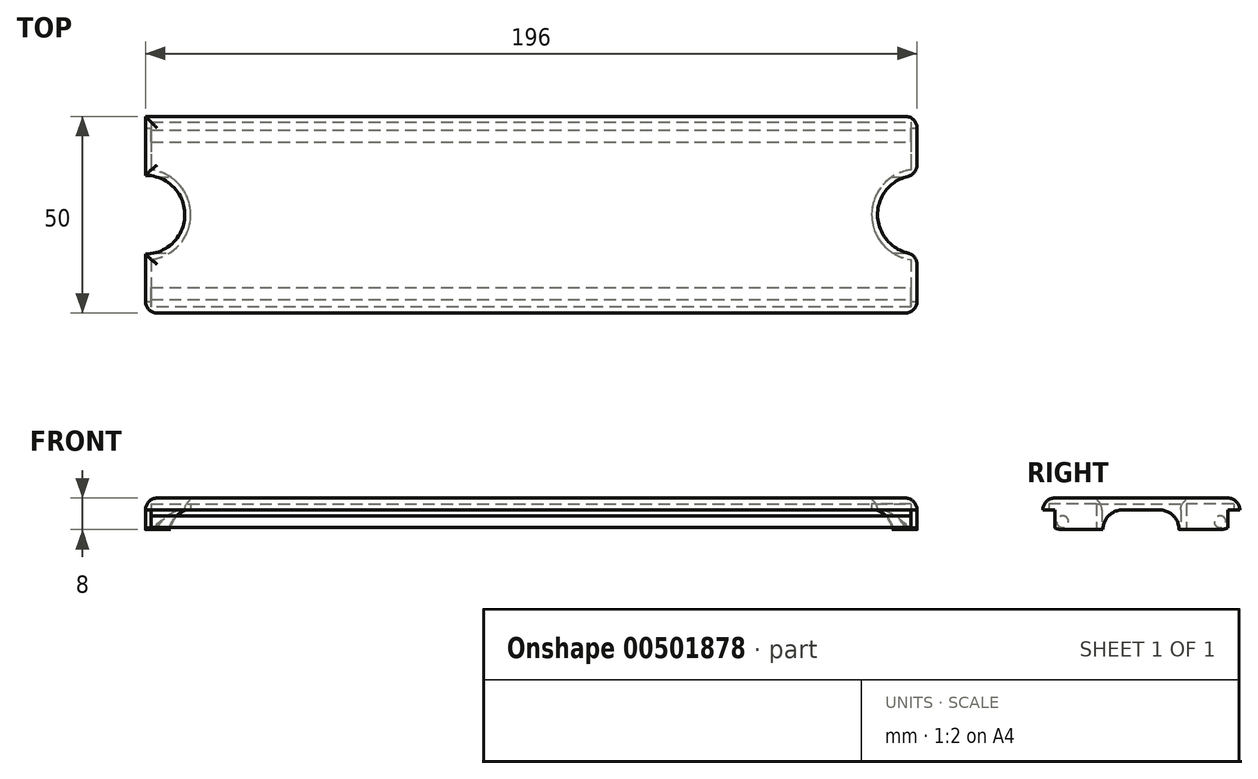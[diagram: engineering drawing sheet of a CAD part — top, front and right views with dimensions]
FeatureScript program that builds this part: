
annotation { "Feature Type Name" : "Feature", "Feature Type Description" : "" }
export const myFeature = defineFeature(function(context is Context, id is Id, definition is map)
    precondition{}
    {
        {
            var Q0;
            Q0=qCreatedBy(makeId("Top.planeOp"),FACE);
            var sketch = newSketch(context, id + "F0", { "sketchPlane" : qUnion([Q0])});
            skLineSegment(sketch, "E0.bottom", {"start": v(-50, 12.24) * mm, "end": v(146, 12.24) * mm});
            skLineSegment(sketch, "E0.top", {"start": v(-50, -37.76) * mm, "end": v(146, -37.76) * mm});
            skLineSegment(sketch, "E0.left", {"start": v(-50, 12.24) * mm, "end": v(-50, -2.76) * mm});
            skLineSegment(sketch, "E0.right", {"start": v(146, 12.24) * mm, "end": v(146, -2.76) * mm});
            skArc(sketch, "E1", {"start": v(-50, -22.76) * mm, "mid": v(-40, -12.76) * mm, "end": v(-50, -2.76) * mm});
            skArc(sketch, "E2", {"start": v(146, -2.76) * mm, "mid": v(136, -12.76) * mm, "end": v(146, -22.76) * mm});
            skLineSegment(sketch, "E3.trimOffspring", {"start": v(-50, -22.76) * mm, "end": v(-50, -37.76) * mm});
            skLineSegment(sketch, "E4", {"start": v(146, -22.76) * mm, "end": v(146, -37.76) * mm});
            skSolve(sketch);
        }
        {
            var Q0;
            Q0=makeQuery(id+"F0.imprint","IMPRINT",FACE,{"disambiguationData":[TD([[makeQuery(id+"F0.imprint","IMPRINT",EDGE,{"derivedFrom":sQuery(id+"F0.wireOp",EDGE,"E0.bottom")}),-1.0]])]});
            extrude(context, id + "F1", {"entities" : qUnion([Q0]), "depth" : 8 * mm});
        }
        {
            var Q0;
            Q0=makeQuery(id+"F1.opExtrude","SWEPT_FACE",FACE,{"disambiguationData":[OSD([sQuery(id+"F0.wireOp",EDGE,"E0.right")])]});
            var sketch = newSketch(context, id + "F2", { "sketchPlane" : qUnion([Q0])});
            skCircle(sketch, "E5", {"center": v(7.24, 2) * mm, "radius": 1.5 * mm});
            skCircle(sketch, "E6", {"center": v(-32.76, 2) * mm, "radius": 1.5 * mm});
            skSolve(sketch);
        }
        {
            var Q0;
            Q0=makeQuery(id+"F1.opExtrude","CAP_FACE",FACE,{"disambiguationData":[OSD([sQuery(id+"F0.wireOp",EDGE,"E0.bottom"),sQuery(id+"F0.wireOp",EDGE,"E0.top"),sQuery(id+"F0.wireOp",EDGE,"E0.left"),sQuery(id+"F0.wireOp",EDGE,"E0.right")])],"isStart":true});
            shell(context, id + "F3", {"entities" : qUnion([Q0]), "thickness" : 1.5 * mm});
        }
        {
            var Q0;
            Q0 = qSketchRegion(id + "F2", true);
            var Q1;
            Q1=makeQuery(id+"F1.opExtrude","SWEPT_FACE",FACE,{"disambiguationData":[OSD([sQuery(id+"F0.wireOp",EDGE,"E0.left")])]});
            extrude(context, id + "F4", {"entities" : qUnion([Q0]), "operationType" : NewBodyOperationType.ADD, "endBound" : BoundingType.UP_TO_SURFACE, "oppositeDirection" : true, "endBoundEntityFace" : qUnion([Q1]), "depth" : 25 * mm});
        }
        {
            var Q0;
            Q0=makeQuery(id+"F1.opExtrude","SWEPT_FACE",FACE,{"disambiguationData":[OSD([sQuery(id+"F0.wireOp",EDGE,"E0.left")])]});
            var sketch = newSketch(context, id + "F5", { "sketchPlane" : qUnion([Q0])});
            skPoint(sketch, "E7.visualSharp", {"position": v(-18.24, 0) * mm});
            skArc(sketch, "E7.filletArc", {"start": v(-18.24, 7) * mm, "mid": v(-16.2, 2.05) * mm, "end": v(-11.24, 0) * mm});
            skLineSegment(sketch, "E8", {"start": v(-18.24, 7) * mm, "end": v(-18.24, 0) * mm});
            skLineSegment(sketch, "E9", {"start": v(-18.24, 0) * mm, "end": v(-11.24, 0) * mm});
            skPoint(sketch, "E10.visualSharp", {"position": v(-12.24, 0) * mm});
            skArc(sketch, "E10.filletArc", {"start": v(-19.24, 0) * mm, "mid": v(-14.3, 2.05) * mm, "end": v(-12.24, 7) * mm});
            skPoint(sketch, "E11.end.orphan", {"position": v(29.67, 8) * mm});
            skLineSegment(sketch, "E12", {"start": v(-12.24, 7) * mm, "end": v(-12.24, 0) * mm});
            skLineSegment(sketch, "E13", {"start": v(-12.24, 0) * mm, "end": v(-19.24, 0) * mm});
            skSolve(sketch);
        }
        {
            var Q0;
            Q0 = qSketchRegion(id + "F5", true);
            extrude(context, id + "F6", {"entities" : qUnion([Q0]), "operationType" : NewBodyOperationType.REMOVE, "endBound" : BoundingType.THROUGH_ALL, "oppositeDirection" : true, "depth" : 25 * mm});
        }
        {
            var Q0;
            Q0=makeQuery(id+"F1.opExtrude","CAP_EDGE",EDGE,{"disambiguationData":[OSD([sQuery(id+"F0.wireOp",EDGE,"E0.top")])],"isStart":false});
            var Q1;
            Q1=makeQuery(id+"F1.opExtrude","CAP_EDGE",EDGE,{"disambiguationData":[OSD([sQuery(id+"F0.wireOp",EDGE,"E0.bottom")])],"isStart":false});
            var Q2;
            Q2=makeQuery(id+"F1.opExtrude","CAP_EDGE",EDGE,{"disambiguationData":[OSD([sQuery(id+"F0.wireOp",EDGE,"E0.right")])],"isStart":false});
            var Q3;
            Q3=makeQuery(id+"F1.opExtrude","CAP_EDGE",EDGE,{"disambiguationData":[OSD([sQuery(id+"F0.wireOp",EDGE,"E4")])],"isStart":false});
            var Q4;
            Q4=makeQuery(id+"F1.opExtrude","CAP_EDGE",EDGE,{"disambiguationData":[OSD([sQuery(id+"F0.wireOp",EDGE,"E2")])],"isStart":false});
            var Q5;
            Q5=makeQuery(id+"F1.opExtrude","CAP_EDGE",EDGE,{"disambiguationData":[OSD([sQuery(id+"F0.wireOp",EDGE,"E0.left")])],"isStart":false});
            var Q6;
            Q6=makeQuery(id+"F1.opExtrude","CAP_EDGE",EDGE,{"disambiguationData":[OSD([sQuery(id+"F0.wireOp",EDGE,"E1")])],"isStart":false});
            var Q7;
            Q7=makeQuery(id+"F1.opExtrude","CAP_EDGE",EDGE,{"disambiguationData":[OSD([sQuery(id+"F0.wireOp",EDGE,"E3.trimOffspring")])],"isStart":false});
            var Q8;
            Q8=makeQuery(id+"F1.opExtrude","SWEPT_EDGE",EDGE,{"disambiguationData":[OSD([sQuery(id+"F0.wireOp",EDGE,"E0.top"),sQuery(id+"F0.wireOp",EDGE,"E4")])]});
            var Q9;
            Q9=makeQuery(id+"F1.opExtrude","SWEPT_EDGE",EDGE,{"disambiguationData":[OSD([sQuery(id+"F0.wireOp",EDGE,"E0.bottom"),sQuery(id+"F0.wireOp",EDGE,"E0.right")])]});
            var Q10;
            Q10=makeQuery(id+"F1.opExtrude","SWEPT_EDGE",EDGE,{"disambiguationData":[OSD([sQuery(id+"F0.wireOp",EDGE,"E0.top"),sQuery(id+"F0.wireOp",EDGE,"E3.trimOffspring")])]});
            var Q11;
            Q11=makeQuery(id+"F1.opExtrude","SWEPT_EDGE",EDGE,{"disambiguationData":[OSD([sQuery(id+"F0.wireOp",EDGE,"E0.right"),sQuery(id+"F0.wireOp",EDGE,"E2")])]});
            var Q12;
            Q12=makeQuery(id+"F1.opExtrude","SWEPT_EDGE",EDGE,{"disambiguationData":[OSD([sQuery(id+"F0.wireOp",EDGE,"E2"),sQuery(id+"F0.wireOp",EDGE,"E4")])]});
            fillet(context, id + "F7", {"entities" : qUnion([Q0, Q1, Q2, Q3, Q4, Q5, Q6, Q7, Q8, Q9, Q10, Q11, Q12]), "radius" : 3 * mm, "tangentPropagation" : true, "allowEdgeOverflow" : false});
        }
        {
            var Q0;
            Q0=makeQuery(id+"F1.opExtrude","SWEPT_FACE",FACE,{"disambiguationData":[OSD([sQuery(id+"F0.wireOp",EDGE,"E4")])]});
            var sketch = newSketch(context, id + "F8", { "sketchPlane" : qUnion([Q0])});
            skLineSegment(sketch, "E14.bottom", {"start": v(-22.51, 0) * mm, "end": v(-3.17, 0) * mm});
            skLineSegment(sketch, "E14.top", {"start": v(-17.51, 5) * mm, "end": v(-8.17, 5) * mm});
            skLineSegment(sketch, "E14.left", {"start": v(-22.51, 0) * mm, "end": v(-22.51, 0) * mm});
            skLineSegment(sketch, "E14.right", {"start": v(-3.17, 0) * mm, "end": v(-3.17, 0) * mm});
            skPoint(sketch, "E15.visualSharp", {"position": v(-22.51, 5) * mm});
            skArc(sketch, "E15.filletArc", {"start": v(-17.51, 5) * mm, "mid": v(-21.05, 3.54) * mm, "end": v(-22.51, 0) * mm});
            skPoint(sketch, "E16.visualSharp", {"position": v(-3.17, 5) * mm});
            skArc(sketch, "E16.filletArc", {"start": v(-3.17, 0) * mm, "mid": v(-4.63, 3.54) * mm, "end": v(-8.17, 5) * mm});
            skSolve(sketch);
        }
        {
            var Q0;
            Q0 = qSketchRegion(id + "F8", true);
            extrude(context, id + "F9", {"entities" : qUnion([Q0]), "operationType" : NewBodyOperationType.REMOVE, "endBound" : BoundingType.THROUGH_ALL, "oppositeDirection" : true, "depth" : 25 * mm});
        }
        {
            var Q0;
            Q0=makeQuery(id+"F1.opExtrude","SWEPT_FACE",FACE,{"disambiguationData":[OSD([sQuery(id+"F0.wireOp",EDGE,"E4")])]});
            var sketch = newSketch(context, id + "F10", { "sketchPlane" : qUnion([Q0])});
            skPoint(sketch, "E17.visualSharp", {"position": v(-37.76, 0) * mm});
            skArc(sketch, "E17.filletArc", {"start": v(-34.76, 0.42) * mm, "mid": v(-33.78, 0.1) * mm, "end": v(-32.76, 0) * mm});
            skPoint(sketch, "E18.visualSharp", {"position": v(12.24, 0) * mm});
            skPoint(sketch, "E18.filletArc.end.orphan", {"position": v(12.24, 5) * mm});
            skPoint(sketch, "E19.start.orphan", {"position": v(7.75, 0) * mm});
            skLineSegment(sketch, "E20", {"start": v(-37.76, 0) * mm, "end": v(-32.76, 0) * mm});
            skLineSegment(sketch, "E21", {"start": v(-37.76, 0) * mm, "end": v(-37.76, 5) * mm});
            skLineSegment(sketch, "E22", {"start": v(12.24, 5) * mm, "end": v(12.24, 5) * mm});
            skLineSegment(sketch, "E23", {"start": v(7.75, 0) * mm, "end": v(7.24, 0) * mm});
            skPoint(sketch, "E24.start.orphan", {"position": v(7.24, 0) * mm});
            skArc(sketch, "E25.filletArc", {"start": v(7.24, 0) * mm, "mid": v(8.26, 0.1) * mm, "end": v(9.24, 0.42) * mm});
            skLineSegment(sketch, "E26", {"start": v(12.24, 5) * mm, "end": v(12.24, 0) * mm});
            skLineSegment(sketch, "E27", {"start": v(12.24, 0) * mm, "end": v(7.24, 0) * mm});
            skLineSegment(sketch, "E28", {"start": v(12.24, 5) * mm, "end": v(9.24, 5) * mm});
            skLineSegment(sketch, "E29", {"start": v(9.24, 0.42) * mm, "end": v(9.24, 5) * mm});
            skLineSegment(sketch, "E30", {"start": v(-37.76, 5) * mm, "end": v(-34.76, 5) * mm});
            skLineSegment(sketch, "E31", {"start": v(-34.76, 5) * mm, "end": v(-34.76, 0.42) * mm});
            skSolve(sketch);
        }
        {
            var Q0;
            Q0 = qSketchRegion(id + "F10", true);
            extrude(context, id + "F11", {"entities" : qUnion([Q0]), "operationType" : NewBodyOperationType.REMOVE, "endBound" : BoundingType.THROUGH_ALL, "oppositeDirection" : true, "depth" : 25 * mm});
        }
    });
